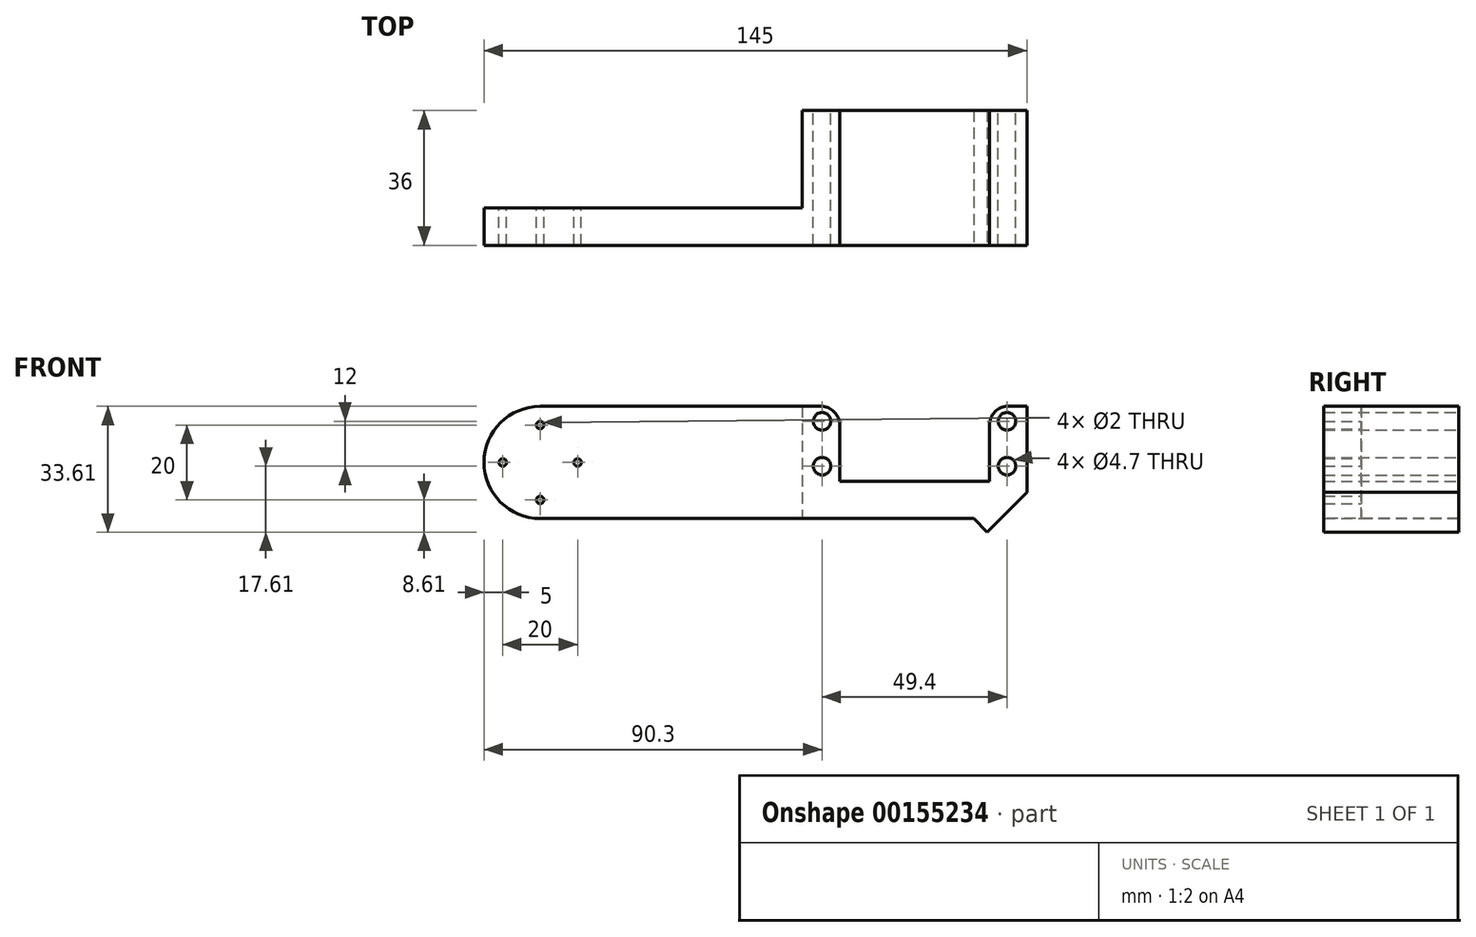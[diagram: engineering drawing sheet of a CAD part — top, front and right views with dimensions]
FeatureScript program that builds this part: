
annotation { "Feature Type Name" : "Feature", "Feature Type Description" : "" }
export const myFeature = defineFeature(function(context is Context, id is Id, definition is map)
    precondition{}
    {
        {
            var Q0;
            Q0=qCreatedBy(makeId("Front.planeOp"),FACE);
            var sketch = newSketch(context, id + "F0", { "sketchPlane" : qUnion([Q0])});
            skArc(sketch, "E0", {"start": v(0, 15) * mm, "mid": v(-15, 0) * mm, "end": v(0, -15) * mm});
            skLineSegment(sketch, "E1.bottom", {"start": v(0, 15) * mm, "end": v(80, 15) * mm});
            skLineSegment(sketch, "E1.top", {"start": v(0, -15) * mm, "end": v(130, -15) * mm});
            skLineSegment(sketch, "E1.right", {"start": v(130, 15) * mm, "end": v(130, -15) * mm});
            skCircle(sketch, "E2", {"center": v(0, 10) * mm, "radius": 1 * mm});
            skCircle(sketch, "E3", {"center": v(0, -10) * mm, "radius": 1 * mm});
            skCircle(sketch, "E4", {"center": v(-10, 0) * mm, "radius": 1 * mm});
            skCircle(sketch, "E5", {"center": v(10, 0) * mm, "radius": 1 * mm});
            skLineSegment(sketch, "E6.top", {"start": v(80, -5) * mm, "end": v(120, -5) * mm});
            skLineSegment(sketch, "E6.left", {"start": v(80, 15) * mm, "end": v(80, -5) * mm});
            skLineSegment(sketch, "E6.right", {"start": v(120, 15) * mm, "end": v(120, -5) * mm});
            skLineSegment(sketch, "E7.trimOffspring", {"start": v(120, 15) * mm, "end": v(130, 15) * mm});
            skCircle(sketch, "E8", {"center": v(124.7, -1) * mm, "radius": 2.35 * mm});
            skCircle(sketch, "E9", {"center": v(124.7, 11) * mm, "radius": 2.35 * mm});
            skCircle(sketch, "E10", {"center": v(75.3, 11) * mm, "radius": 2.35 * mm});
            skCircle(sketch, "E11", {"center": v(75.3, -1) * mm, "radius": 2.35 * mm});
            skSolve(sketch);
        }
        {
            var Q0;
            Q0 = qSketchRegion(id + "F0", true);
            extrude(context, id + "F1", {"entities" : qUnion([Q0]), "depth" : 36 * mm});
        }
        {
            var Q0;
            Q0=makeQuery(id+"F1.opExtrude","CAP_FACE",FACE,{"disambiguationData":[OSD([sQuery(id+"F0.wireOp",EDGE,"E0"),sQuery(id+"F0.wireOp",EDGE,"E1.bottom"),sQuery(id+"F0.wireOp",EDGE,"E1.top"),sQuery(id+"F0.wireOp",EDGE,"E1.right"),sQuery(id+"F0.wireOp",EDGE,"E2"),sQuery(id+"F0.wireOp",EDGE,"E3"),sQuery(id+"F0.wireOp",EDGE,"E4"),sQuery(id+"F0.wireOp",EDGE,"E5"),sQuery(id+"F0.wireOp",EDGE,"E6.top"),sQuery(id+"F0.wireOp",EDGE,"E6.left"),sQuery(id+"F0.wireOp",EDGE,"E6.right"),sQuery(id+"F0.wireOp",EDGE,"E7.trimOffspring"),sQuery(id+"F0.wireOp",EDGE,"E8"),sQuery(id+"F0.wireOp",EDGE,"E9"),sQuery(id+"F0.wireOp",EDGE,"E10"),sQuery(id+"F0.wireOp",EDGE,"E11")])],"isStart":true});
            var sketch = newSketch(context, id + "F2", { "sketchPlane" : qUnion([Q0])});
            skLineSegment(sketch, "E12.bottom", {"start": v(-70, 15) * mm, "end": v(28.14, 15) * mm});
            skLineSegment(sketch, "E12.top", {"start": v(-70, -15) * mm, "end": v(28.14, -15) * mm});
            skLineSegment(sketch, "E12.left", {"start": v(-70, 15) * mm, "end": v(-70, -15) * mm});
            skLineSegment(sketch, "E12.right", {"start": v(28.14, 15) * mm, "end": v(28.14, -15) * mm});
            skSolve(sketch);
        }
        {
            var Q0;
            Q0 = qSketchRegion(id + "F2", true);
            extrude(context, id + "F3", {"entities" : qUnion([Q0]), "operationType" : NewBodyOperationType.REMOVE, "oppositeDirection" : true, "depth" : 26 * mm});
        }
        {
            var Q0;
            Q0=makeQuery(id+"F1.opExtrude","SWEPT_EDGE",EDGE,{"disambiguationData":[OSD([sQuery(id+"F0.wireOp",EDGE,"E1.bottom"),sQuery(id+"F0.wireOp",EDGE,"E6.left")])]});
            var Q1;
            Q1=makeQuery(id+"F1.opExtrude","SWEPT_EDGE",EDGE,{"disambiguationData":[OSD([sQuery(id+"F0.wireOp",EDGE,"E6.right"),sQuery(id+"F0.wireOp",EDGE,"E7.trimOffspring")])]});
            fillet(context, id + "F4", {"entities" : qUnion([Q0, Q1]), "radius" : 5 * mm, "tangentPropagation" : true, "allowEdgeOverflow" : false});
        }
        {
            var Q0;
            Q0=makeQuery(id+"F1.opExtrude","SWEPT_EDGE",EDGE,{"disambiguationData":[OSD([sQuery(id+"F0.wireOp",EDGE,"E1.top"),sQuery(id+"F0.wireOp",EDGE,"E1.right")])]});
            chamfer(context, id + "F5", {"entities" : qUnion([Q0]), "width" : 7 * mm, "tangentPropagation" : true});
        }
        {
            var Q0;
            Q0=makeQuery(id+"F1.opExtrude","CAP_FACE",FACE,{"disambiguationData":[OSD([sQuery(id+"F0.wireOp",EDGE,"E0"),sQuery(id+"F0.wireOp",EDGE,"E1.bottom"),sQuery(id+"F0.wireOp",EDGE,"E1.top"),sQuery(id+"F0.wireOp",EDGE,"E1.right"),sQuery(id+"F0.wireOp",EDGE,"E2"),sQuery(id+"F0.wireOp",EDGE,"E3"),sQuery(id+"F0.wireOp",EDGE,"E4"),sQuery(id+"F0.wireOp",EDGE,"E5"),sQuery(id+"F0.wireOp",EDGE,"E6.top"),sQuery(id+"F0.wireOp",EDGE,"E6.left"),sQuery(id+"F0.wireOp",EDGE,"E6.right"),sQuery(id+"F0.wireOp",EDGE,"E7.trimOffspring"),sQuery(id+"F0.wireOp",EDGE,"E8"),sQuery(id+"F0.wireOp",EDGE,"E9"),sQuery(id+"F0.wireOp",EDGE,"E10"),sQuery(id+"F0.wireOp",EDGE,"E11")])],"isStart":false});
            var sketch = newSketch(context, id + "F6", { "sketchPlane" : qUnion([Q0])});
            skLineSegment(sketch, "E13", {"start": v(130, -8) * mm, "end": v(119.4, -18.6) * mm});
            skLineSegment(sketch, "E14", {"start": v(119.4, -18.6) * mm, "end": v(115.79, -15) * mm});
            skLineSegment(sketch, "E15", {"start": v(115.79, -15) * mm, "end": v(123, -15) * mm});
            skSolve(sketch);
        }
        {
            var Q0;
            Q0 = qSketchRegion(id + "F6", true);
            extrude(context, id + "F7", {"entities" : qUnion([Q0]), "operationType" : NewBodyOperationType.ADD, "oppositeDirection" : true, "depth" : 36 * mm});
        }
    });
